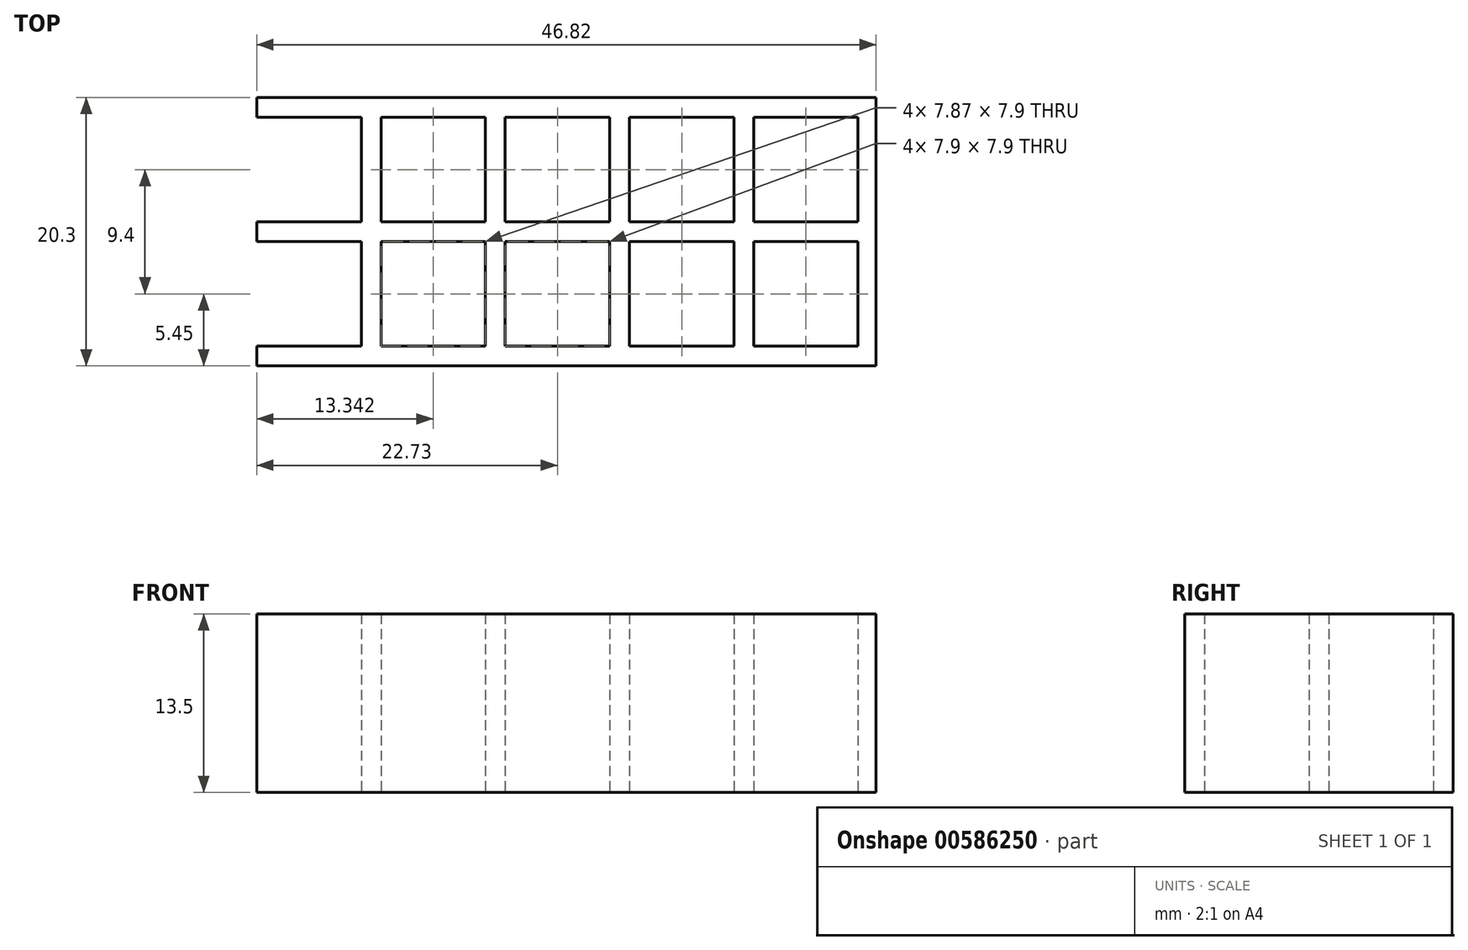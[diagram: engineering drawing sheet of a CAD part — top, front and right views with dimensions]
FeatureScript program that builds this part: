
annotation { "Feature Type Name" : "Feature", "Feature Type Description" : "" }
export const myFeature = defineFeature(function(context is Context, id is Id, definition is map)
    precondition{}
    {
        {
            var Q0;
            Q0=qCreatedBy(makeId("Top.planeOp"),FACE);
            var sketch = newSketch(context, id + "F0", { "sketchPlane" : qUnion([Q0])});
            skLineSegment(sketch, "E0.bottom", {"start": v(-26.67, 20.52) * mm, "end": v(26.68, 20.52) * mm});
            skLineSegment(sketch, "E0.top", {"start": v(-26.68, -20.52) * mm, "end": v(26.67, -20.52) * mm});
            skLineSegment(sketch, "E0.left", {"start": v(-26.67, 20.52) * mm, "end": v(-26.68, -20.53) * mm});
            skLineSegment(sketch, "E0.right", {"start": v(26.68, 20.52) * mm, "end": v(26.67, -20.52) * mm});
            skPoint(sketch, "E0.middle", {"position": v(0, 0) * mm});
            skLineSegment(sketch, "E1.bottom", {"start": v(-26.68, 0.75) * mm, "end": v(26.68, 0.75) * mm});
            skLineSegment(sketch, "E1.top", {"start": v(-26.68, -0.75) * mm, "end": v(26.68, -0.75) * mm});
            skLineSegment(sketch, "E1.left", {"start": v(-26.67, 0.75) * mm, "end": v(-26.67, -0.75) * mm});
            skLineSegment(sketch, "E1.right", {"start": v(26.67, 0.75) * mm, "end": v(26.67, -0.75) * mm});
            skLineSegment(sketch, "E2.bottom", {"start": v(-26.67, -0.75) * mm, "end": v(26.67, -0.75) * mm});
            skLineSegment(sketch, "E2.top", {"start": v(-26.67, -8.65) * mm, "end": v(26.68, -8.65) * mm});
            skLineSegment(sketch, "E2.left", {"start": v(-26.68, -0.75) * mm, "end": v(-26.68, -8.65) * mm});
            skLineSegment(sketch, "E2.right", {"start": v(26.67, -0.75) * mm, "end": v(26.67, -8.65) * mm});
            skLineSegment(sketch, "E3.bottom", {"start": v(-26.67, -8.65) * mm, "end": v(26.67, -8.65) * mm});
            skLineSegment(sketch, "E3.top", {"start": v(-26.68, -10.15) * mm, "end": v(26.68, -10.15) * mm});
            skLineSegment(sketch, "E3.left", {"start": v(-26.67, -8.65) * mm, "end": v(-26.67, -10.15) * mm});
            skLineSegment(sketch, "E3.right", {"start": v(26.67, -8.65) * mm, "end": v(26.67, -10.15) * mm});
            skLineSegment(sketch, "E4", {"start": v(-26.67, -10.15) * mm, "end": v(-26.67, -8.65) * mm});
            skLineSegment(sketch, "E5.top", {"start": v(-26.68, 8.65) * mm, "end": v(26.68, 8.65) * mm});
            skLineSegment(sketch, "E5.left", {"start": v(-26.68, 0.75) * mm, "end": v(-26.68, 8.65) * mm});
            skLineSegment(sketch, "E5.right", {"start": v(26.68, 0.75) * mm, "end": v(26.68, 8.65) * mm});
            skLineSegment(sketch, "E6", {"start": v(-26.68, 8.65) * mm, "end": v(-26.68, 0.75) * mm});
            skLineSegment(sketch, "E7.top", {"start": v(-26.68, 10.15) * mm, "end": v(26.68, 10.15) * mm});
            skLineSegment(sketch, "E7.left", {"start": v(-26.68, 8.65) * mm, "end": v(-26.68, 10.15) * mm});
            skLineSegment(sketch, "E7.right", {"start": v(26.68, 8.65) * mm, "end": v(26.68, 10.15) * mm});
            skLineSegment(sketch, "E8.bottom", {"start": v(-26.67, 20.52) * mm, "end": v(-18.78, 20.52) * mm});
            skLineSegment(sketch, "E8.top", {"start": v(-26.67, -20.52) * mm, "end": v(-18.78, -20.52) * mm});
            skLineSegment(sketch, "E8.left", {"start": v(-26.67, 20.52) * mm, "end": v(-26.67, -20.52) * mm});
            skLineSegment(sketch, "E8.right", {"start": v(-18.78, 20.52) * mm, "end": v(-18.78, -20.53) * mm});
            skLineSegment(sketch, "E9.bottom", {"start": v(-18.78, 20.52) * mm, "end": v(-17.27, 20.52) * mm});
            skLineSegment(sketch, "E9.top", {"start": v(-18.78, -20.52) * mm, "end": v(-17.27, -20.52) * mm});
            skLineSegment(sketch, "E9.left", {"start": v(-18.78, 20.52) * mm, "end": v(-18.78, -20.52) * mm});
            skLineSegment(sketch, "E9.right", {"start": v(-17.27, 20.52) * mm, "end": v(-17.27, -20.53) * mm});
            skLineSegment(sketch, "E10.bottom", {"start": v(-17.27, 20.52) * mm, "end": v(-9.4, 20.52) * mm});
            skLineSegment(sketch, "E10.top", {"start": v(-17.27, -20.52) * mm, "end": v(-9.4, -20.52) * mm});
            skLineSegment(sketch, "E10.left", {"start": v(-17.27, 20.52) * mm, "end": v(-17.27, -20.52) * mm});
            skLineSegment(sketch, "E10.right", {"start": v(-9.4, 20.52) * mm, "end": v(-9.4, -20.53) * mm});
            skLineSegment(sketch, "E11.bottom", {"start": v(-9.4, 20.52) * mm, "end": v(-7.9, 20.52) * mm});
            skLineSegment(sketch, "E11.top", {"start": v(-9.4, -20.52) * mm, "end": v(-7.9, -20.52) * mm});
            skLineSegment(sketch, "E11.right", {"start": v(-7.9, 20.52) * mm, "end": v(-7.9, -20.53) * mm});
            skLineSegment(sketch, "E12.bottom", {"start": v(-7.9, 20.52) * mm, "end": v(0, 20.52) * mm});
            skLineSegment(sketch, "E12.top", {"start": v(-7.9, -20.52) * mm, "end": v(0, -20.52) * mm});
            skLineSegment(sketch, "E12.right", {"start": v(0, 20.52) * mm, "end": v(0, -20.52) * mm});
            skLineSegment(sketch, "E13.bottom", {"start": v(0, 20.52) * mm, "end": v(1.5, 20.52) * mm});
            skLineSegment(sketch, "E13.top", {"start": v(0, -20.52) * mm, "end": v(1.5, -20.52) * mm});
            skLineSegment(sketch, "E13.right", {"start": v(1.5, 20.52) * mm, "end": v(1.5, -20.53) * mm});
            skLineSegment(sketch, "E14.bottom", {"start": v(1.5, 20.52) * mm, "end": v(9.4, 20.52) * mm});
            skLineSegment(sketch, "E14.top", {"start": v(1.5, -20.52) * mm, "end": v(9.4, -20.52) * mm});
            skLineSegment(sketch, "E14.left", {"start": v(1.5, 20.52) * mm, "end": v(1.5, -20.52) * mm});
            skLineSegment(sketch, "E14.right", {"start": v(9.4, 20.52) * mm, "end": v(9.4, -20.53) * mm});
            skLineSegment(sketch, "E15.bottom", {"start": v(9.4, 20.52) * mm, "end": v(10.9, 20.52) * mm});
            skLineSegment(sketch, "E15.top", {"start": v(9.4, -20.52) * mm, "end": v(10.9, -20.52) * mm});
            skLineSegment(sketch, "E15.left", {"start": v(9.4, 20.52) * mm, "end": v(9.4, -20.52) * mm});
            skLineSegment(sketch, "E15.right", {"start": v(10.9, 20.52) * mm, "end": v(10.9, -20.53) * mm});
            skLineSegment(sketch, "E16", {"start": v(10.9, 20.52) * mm, "end": v(9.4, 20.52) * mm, "construction": true});
            skLineSegment(sketch, "E17.bottom", {"start": v(10.9, 20.52) * mm, "end": v(18.78, 20.52) * mm});
            skLineSegment(sketch, "E17.top", {"start": v(10.9, -20.52) * mm, "end": v(18.78, -20.52) * mm});
            skLineSegment(sketch, "E17.left", {"start": v(10.9, 20.52) * mm, "end": v(10.9, -20.52) * mm});
            skLineSegment(sketch, "E17.right", {"start": v(18.78, 20.52) * mm, "end": v(18.78, -20.53) * mm});
            skLineSegment(sketch, "E18.bottom", {"start": v(18.78, 20.52) * mm, "end": v(20.14, 20.52) * mm});
            skLineSegment(sketch, "E18.top", {"start": v(18.78, -20.52) * mm, "end": v(20.14, -20.52) * mm});
            skLineSegment(sketch, "E18.left", {"start": v(18.78, 20.52) * mm, "end": v(18.78, -20.52) * mm});
            skLineSegment(sketch, "E18.right", {"start": v(20.14, 20.52) * mm, "end": v(20.14, -20.52) * mm});
            skSolve(sketch);
        }
        {
            var Q0;
            {var subQ5=sQuery(id+"F0.wireOp",EDGE,"E9.bottom");Q0=makeQuery(id+"F0.imprint","IMPRINT",FACE,{"disambiguationData":[TD([[makeQuery(id+"F0.imprint","IMPRINT",EDGE,{"derivedFrom":subQ5}),-1.0]])]});}
            var Q1;
            {var subQ0=sQuery(id+"F0.wireOp",EDGE,"E9.left");var subQ1=sQuery(id+"F0.wireOp",EDGE,"E5.top");var subQ2=makeQuery(id+"F0.imprint","INTERSECT",VERTEX,{"derivedFrom":[subQ1,subQ0]});Q1=makeQuery(id+"F0.imprint","IMPRINT",FACE,{"disambiguationData":[TD([[makeQuery(id+"F0.imprint","IMPRINT",EDGE,{"disambiguationData":[TD([[subQ2,-1.0]])],"derivedFrom":subQ1}),1.0]])]});}
            var Q2;
            {var subQ0=sQuery(id+"F0.wireOp",EDGE,"E8.left");var subQ1=sQuery(id+"F0.wireOp",EDGE,"E5.top");var subQ2=makeQuery(id+"F0.imprint","INTERSECT",VERTEX,{"derivedFrom":[subQ1,subQ0]});Q2=makeQuery(id+"F0.imprint","IMPRINT",FACE,{"disambiguationData":[TD([[makeQuery(id+"F0.imprint","IMPRINT",EDGE,{"disambiguationData":[TD([[subQ2,-1.0]])],"derivedFrom":subQ1}),1.0]])]});}
            var Q3;
            {var subQ0=sQuery(id+"F0.wireOp",EDGE,"E9.left");var subQ1=sQuery(id+"F0.wireOp",EDGE,"E1.bottom");var subQ2=makeQuery(id+"F0.imprint","INTERSECT",VERTEX,{"derivedFrom":[subQ1,subQ0]});Q3=makeQuery(id+"F0.imprint","IMPRINT",FACE,{"disambiguationData":[TD([[makeQuery(id+"F0.imprint","IMPRINT",EDGE,{"disambiguationData":[TD([[subQ2,-1.0]])],"derivedFrom":subQ1}),1.0]])]});}
            var Q4;
            {var subQ0=sQuery(id+"F0.wireOp",EDGE,"E9.left");var subQ1=sQuery(id+"F0.wireOp",EDGE,"E2.bottom");var subQ2=makeQuery(id+"F0.imprint","INTERSECT",VERTEX,{"derivedFrom":[subQ1,subQ0]});Q4=makeQuery(id+"F0.imprint","IMPRINT",FACE,{"disambiguationData":[TD([[makeQuery(id+"F0.imprint","IMPRINT",EDGE,{"disambiguationData":[TD([[subQ2,-1.0]])],"derivedFrom":subQ1}),1.0]])]});}
            var Q5;
            {var subQ0=sQuery(id+"F0.wireOp",EDGE,"E8.left");var subQ1=sQuery(id+"F0.wireOp",EDGE,"E2.bottom");var subQ2=makeQuery(id+"F0.imprint","INTERSECT",VERTEX,{"derivedFrom":[subQ1,subQ0]});Q5=makeQuery(id+"F0.imprint","IMPRINT",FACE,{"disambiguationData":[TD([[makeQuery(id+"F0.imprint","IMPRINT",EDGE,{"disambiguationData":[TD([[subQ2,-1.0]])],"derivedFrom":subQ1}),1.0]])]});}
            var Q6;
            {var subQ0=sQuery(id+"F0.wireOp",EDGE,"E9.left");var subQ1=sQuery(id+"F0.wireOp",EDGE,"E2.bottom");var subQ2=makeQuery(id+"F0.imprint","INTERSECT",VERTEX,{"derivedFrom":[subQ1,subQ0]});Q6=makeQuery(id+"F0.imprint","IMPRINT",FACE,{"disambiguationData":[TD([[makeQuery(id+"F0.imprint","IMPRINT",EDGE,{"disambiguationData":[TD([[subQ2,-1.0]])],"derivedFrom":subQ1}),-1.0]])]});}
            var Q7;
            {var subQ0=sQuery(id+"F0.wireOp",EDGE,"E9.left");var subQ1=sQuery(id+"F0.wireOp",EDGE,"E3.bottom");var subQ2=makeQuery(id+"F0.imprint","INTERSECT",VERTEX,{"derivedFrom":[subQ1,subQ0]});Q7=makeQuery(id+"F0.imprint","IMPRINT",FACE,{"disambiguationData":[TD([[makeQuery(id+"F0.imprint","IMPRINT",EDGE,{"disambiguationData":[TD([[subQ2,-1.0]])],"derivedFrom":subQ1}),-1.0]])]});}
            var Q8;
            {var subQ0=sQuery(id+"F0.wireOp",EDGE,"E8.left");var subQ1=sQuery(id+"F0.wireOp",EDGE,"E3.bottom");var subQ2=makeQuery(id+"F0.imprint","INTERSECT",VERTEX,{"derivedFrom":[subQ1,subQ0]});Q8=makeQuery(id+"F0.imprint","IMPRINT",FACE,{"disambiguationData":[TD([[makeQuery(id+"F0.imprint","IMPRINT",EDGE,{"disambiguationData":[TD([[subQ2,-1.0]])],"derivedFrom":subQ1}),-1.0]])]});}
            var Q9;
            {var subQ5=sQuery(id+"F0.wireOp",EDGE,"E9.top");Q9=makeQuery(id+"F0.imprint","IMPRINT",FACE,{"disambiguationData":[TD([[makeQuery(id+"F0.imprint","IMPRINT",EDGE,{"derivedFrom":subQ5}),1.0]])]});}
            var Q10;
            {var subQ0=sQuery(id+"F0.wireOp",EDGE,"E10.left");var subQ1=sQuery(id+"F0.wireOp",EDGE,"E3.bottom");var subQ2=makeQuery(id+"F0.imprint","INTERSECT",VERTEX,{"derivedFrom":[subQ1,subQ0]});Q10=makeQuery(id+"F0.imprint","IMPRINT",FACE,{"disambiguationData":[TD([[makeQuery(id+"F0.imprint","IMPRINT",EDGE,{"disambiguationData":[TD([[subQ2,-1.0]])],"derivedFrom":subQ1}),-1.0]])]});}
            var Q11;
            {var subQ0=sQuery(id+"F0.wireOp",EDGE,"E10.right");var subQ1=sQuery(id+"F0.wireOp",EDGE,"E3.bottom");var subQ2=makeQuery(id+"F0.imprint","INTERSECT",VERTEX,{"derivedFrom":[subQ1,subQ0]});Q11=makeQuery(id+"F0.imprint","IMPRINT",FACE,{"disambiguationData":[TD([[makeQuery(id+"F0.imprint","IMPRINT",EDGE,{"disambiguationData":[TD([[subQ2,-1.0]])],"derivedFrom":subQ1}),-1.0]])]});}
            var Q12;
            {var subQ0=sQuery(id+"F0.wireOp",EDGE,"E10.right");var subQ1=sQuery(id+"F0.wireOp",EDGE,"E2.bottom");var subQ2=makeQuery(id+"F0.imprint","INTERSECT",VERTEX,{"derivedFrom":[subQ1,subQ0]});Q12=makeQuery(id+"F0.imprint","IMPRINT",FACE,{"disambiguationData":[TD([[makeQuery(id+"F0.imprint","IMPRINT",EDGE,{"disambiguationData":[TD([[subQ2,-1.0]])],"derivedFrom":subQ1}),-1.0]])]});}
            var Q13;
            {var subQ0=sQuery(id+"F0.wireOp",EDGE,"E10.right");var subQ1=sQuery(id+"F0.wireOp",EDGE,"E2.bottom");var subQ2=makeQuery(id+"F0.imprint","INTERSECT",VERTEX,{"derivedFrom":[subQ1,subQ0]});Q13=makeQuery(id+"F0.imprint","IMPRINT",FACE,{"disambiguationData":[TD([[makeQuery(id+"F0.imprint","IMPRINT",EDGE,{"disambiguationData":[TD([[subQ2,-1.0]])],"derivedFrom":subQ1}),1.0]])]});}
            var Q14;
            {var subQ0=sQuery(id+"F0.wireOp",EDGE,"E10.left");var subQ1=sQuery(id+"F0.wireOp",EDGE,"E2.bottom");var subQ2=makeQuery(id+"F0.imprint","INTERSECT",VERTEX,{"derivedFrom":[subQ1,subQ0]});Q14=makeQuery(id+"F0.imprint","IMPRINT",FACE,{"disambiguationData":[TD([[makeQuery(id+"F0.imprint","IMPRINT",EDGE,{"disambiguationData":[TD([[subQ2,-1.0]])],"derivedFrom":subQ1}),1.0]])]});}
            var Q15;
            {var subQ5=sQuery(id+"F0.wireOp",EDGE,"E11.top");Q15=makeQuery(id+"F0.imprint","IMPRINT",FACE,{"disambiguationData":[TD([[makeQuery(id+"F0.imprint","IMPRINT",EDGE,{"derivedFrom":subQ5}),1.0]])]});}
            var Q16;
            {var subQ5=sQuery(id+"F0.wireOp",EDGE,"E11.bottom");Q16=makeQuery(id+"F0.imprint","IMPRINT",FACE,{"disambiguationData":[TD([[makeQuery(id+"F0.imprint","IMPRINT",EDGE,{"derivedFrom":subQ5}),-1.0]])]});}
            var Q17;
            {var subQ0=sQuery(id+"F0.wireOp",EDGE,"E10.right");var subQ1=sQuery(id+"F0.wireOp",EDGE,"E5.top");var subQ2=makeQuery(id+"F0.imprint","INTERSECT",VERTEX,{"derivedFrom":[subQ1,subQ0]});Q17=makeQuery(id+"F0.imprint","IMPRINT",FACE,{"disambiguationData":[TD([[makeQuery(id+"F0.imprint","IMPRINT",EDGE,{"disambiguationData":[TD([[subQ2,-1.0]])],"derivedFrom":subQ1}),1.0]])]});}
            var Q18;
            {var subQ0=sQuery(id+"F0.wireOp",EDGE,"E10.right");var subQ1=sQuery(id+"F0.wireOp",EDGE,"E1.bottom");var subQ2=makeQuery(id+"F0.imprint","INTERSECT",VERTEX,{"derivedFrom":[subQ1,subQ0]});Q18=makeQuery(id+"F0.imprint","IMPRINT",FACE,{"disambiguationData":[TD([[makeQuery(id+"F0.imprint","IMPRINT",EDGE,{"disambiguationData":[TD([[subQ2,-1.0]])],"derivedFrom":subQ1}),1.0]])]});}
            var Q19;
            {var subQ0=sQuery(id+"F0.wireOp",EDGE,"E10.left");var subQ1=sQuery(id+"F0.wireOp",EDGE,"E5.top");var subQ2=makeQuery(id+"F0.imprint","INTERSECT",VERTEX,{"derivedFrom":[subQ1,subQ0]});Q19=makeQuery(id+"F0.imprint","IMPRINT",FACE,{"disambiguationData":[TD([[makeQuery(id+"F0.imprint","IMPRINT",EDGE,{"disambiguationData":[TD([[subQ2,-1.0]])],"derivedFrom":subQ1}),1.0]])]});}
            var Q20;
            {var subQ0=sQuery(id+"F0.wireOp",EDGE,"E11.right");var subQ1=sQuery(id+"F0.wireOp",EDGE,"E5.top");var subQ2=makeQuery(id+"F0.imprint","INTERSECT",VERTEX,{"derivedFrom":[subQ1,subQ0]});Q20=makeQuery(id+"F0.imprint","IMPRINT",FACE,{"disambiguationData":[TD([[makeQuery(id+"F0.imprint","IMPRINT",EDGE,{"disambiguationData":[TD([[subQ2,-1.0]])],"derivedFrom":subQ1}),1.0]])]});}
            var Q21;
            {var subQ0=sQuery(id+"F0.wireOp",EDGE,"E12.right");var subQ1=sQuery(id+"F0.wireOp",EDGE,"E5.top");var subQ2=makeQuery(id+"F0.imprint","INTERSECT",VERTEX,{"derivedFrom":[subQ1,subQ0]});Q21=makeQuery(id+"F0.imprint","IMPRINT",FACE,{"disambiguationData":[TD([[makeQuery(id+"F0.imprint","IMPRINT",EDGE,{"disambiguationData":[TD([[subQ2,-1.0]])],"derivedFrom":subQ1}),1.0]])]});}
            var Q22;
            {var subQ5=sQuery(id+"F0.wireOp",EDGE,"E13.bottom");Q22=makeQuery(id+"F0.imprint","IMPRINT",FACE,{"disambiguationData":[TD([[makeQuery(id+"F0.imprint","IMPRINT",EDGE,{"derivedFrom":subQ5}),-1.0]])]});}
            var Q23;
            {var subQ0=sQuery(id+"F0.wireOp",EDGE,"E12.right");var subQ1=sQuery(id+"F0.wireOp",EDGE,"E1.bottom");var subQ2=makeQuery(id+"F0.imprint","INTERSECT",VERTEX,{"derivedFrom":[subQ1,subQ0]});Q23=makeQuery(id+"F0.imprint","IMPRINT",FACE,{"disambiguationData":[TD([[makeQuery(id+"F0.imprint","IMPRINT",EDGE,{"disambiguationData":[TD([[subQ2,-1.0]])],"derivedFrom":subQ1}),1.0]])]});}
            var Q24;
            {var subQ0=sQuery(id+"F0.wireOp",EDGE,"E11.right");var subQ1=sQuery(id+"F0.wireOp",EDGE,"E2.bottom");var subQ2=makeQuery(id+"F0.imprint","INTERSECT",VERTEX,{"derivedFrom":[subQ1,subQ0]});Q24=makeQuery(id+"F0.imprint","IMPRINT",FACE,{"disambiguationData":[TD([[makeQuery(id+"F0.imprint","IMPRINT",EDGE,{"disambiguationData":[TD([[subQ2,-1.0]])],"derivedFrom":subQ1}),1.0]])]});}
            var Q25;
            {var subQ0=sQuery(id+"F0.wireOp",EDGE,"E12.right");var subQ1=sQuery(id+"F0.wireOp",EDGE,"E2.bottom");var subQ2=makeQuery(id+"F0.imprint","INTERSECT",VERTEX,{"derivedFrom":[subQ1,subQ0]});Q25=makeQuery(id+"F0.imprint","IMPRINT",FACE,{"disambiguationData":[TD([[makeQuery(id+"F0.imprint","IMPRINT",EDGE,{"disambiguationData":[TD([[subQ2,-1.0]])],"derivedFrom":subQ1}),1.0]])]});}
            var Q26;
            {var subQ0=sQuery(id+"F0.wireOp",EDGE,"E12.right");var subQ1=sQuery(id+"F0.wireOp",EDGE,"E2.bottom");var subQ2=makeQuery(id+"F0.imprint","INTERSECT",VERTEX,{"derivedFrom":[subQ1,subQ0]});Q26=makeQuery(id+"F0.imprint","IMPRINT",FACE,{"disambiguationData":[TD([[makeQuery(id+"F0.imprint","IMPRINT",EDGE,{"disambiguationData":[TD([[subQ2,-1.0]])],"derivedFrom":subQ1}),-1.0]])]});}
            var Q27;
            {var subQ0=sQuery(id+"F0.wireOp",EDGE,"E12.right");var subQ1=sQuery(id+"F0.wireOp",EDGE,"E3.bottom");var subQ2=makeQuery(id+"F0.imprint","INTERSECT",VERTEX,{"derivedFrom":[subQ1,subQ0]});Q27=makeQuery(id+"F0.imprint","IMPRINT",FACE,{"disambiguationData":[TD([[makeQuery(id+"F0.imprint","IMPRINT",EDGE,{"disambiguationData":[TD([[subQ2,-1.0]])],"derivedFrom":subQ1}),-1.0]])]});}
            var Q28;
            {var subQ0=sQuery(id+"F0.wireOp",EDGE,"E11.right");var subQ1=sQuery(id+"F0.wireOp",EDGE,"E3.bottom");var subQ2=makeQuery(id+"F0.imprint","INTERSECT",VERTEX,{"derivedFrom":[subQ1,subQ0]});Q28=makeQuery(id+"F0.imprint","IMPRINT",FACE,{"disambiguationData":[TD([[makeQuery(id+"F0.imprint","IMPRINT",EDGE,{"disambiguationData":[TD([[subQ2,-1.0]])],"derivedFrom":subQ1}),-1.0]])]});}
            var Q29;
            {var subQ5=sQuery(id+"F0.wireOp",EDGE,"E13.top");Q29=makeQuery(id+"F0.imprint","IMPRINT",FACE,{"disambiguationData":[TD([[makeQuery(id+"F0.imprint","IMPRINT",EDGE,{"derivedFrom":subQ5}),1.0]])]});}
            var Q30;
            {var subQ0=sQuery(id+"F0.wireOp",EDGE,"E14.left");var subQ1=sQuery(id+"F0.wireOp",EDGE,"E3.bottom");var subQ2=makeQuery(id+"F0.imprint","INTERSECT",VERTEX,{"derivedFrom":[subQ1,subQ0]});Q30=makeQuery(id+"F0.imprint","IMPRINT",FACE,{"disambiguationData":[TD([[makeQuery(id+"F0.imprint","IMPRINT",EDGE,{"disambiguationData":[TD([[subQ2,-1.0]])],"derivedFrom":subQ1}),-1.0]])]});}
            var Q31;
            {var subQ5=sQuery(id+"F0.wireOp",EDGE,"E15.top");Q31=makeQuery(id+"F0.imprint","IMPRINT",FACE,{"disambiguationData":[TD([[makeQuery(id+"F0.imprint","IMPRINT",EDGE,{"derivedFrom":subQ5}),1.0]])]});}
            var Q32;
            {var subQ5=sQuery(id+"F0.wireOp",EDGE,"E18.top");Q32=makeQuery(id+"F0.imprint","IMPRINT",FACE,{"disambiguationData":[TD([[makeQuery(id+"F0.imprint","IMPRINT",EDGE,{"derivedFrom":subQ5}),1.0]])]});}
            var Q33;
            {var subQ0=sQuery(id+"F0.wireOp",EDGE,"E3.right");Q33=makeQuery(id+"F0.imprint","IMPRINT",FACE,{"disambiguationData":[TD([[makeQuery(id+"F0.imprint","IMPRINT",EDGE,{"derivedFrom":subQ0}),-1.0]])]});}
            var Q34;
            {var subQ0=sQuery(id+"F0.wireOp",EDGE,"E17.left");var subQ1=sQuery(id+"F0.wireOp",EDGE,"E3.bottom");var subQ2=makeQuery(id+"F0.imprint","INTERSECT",VERTEX,{"derivedFrom":[subQ1,subQ0]});Q34=makeQuery(id+"F0.imprint","IMPRINT",FACE,{"disambiguationData":[TD([[makeQuery(id+"F0.imprint","IMPRINT",EDGE,{"disambiguationData":[TD([[subQ2,-1.0]])],"derivedFrom":subQ1}),-1.0]])]});}
            var Q35;
            {var subQ0=sQuery(id+"F0.wireOp",EDGE,"E18.left");var subQ1=sQuery(id+"F0.wireOp",EDGE,"E3.bottom");var subQ2=makeQuery(id+"F0.imprint","INTERSECT",VERTEX,{"derivedFrom":[subQ1,subQ0]});Q35=makeQuery(id+"F0.imprint","IMPRINT",FACE,{"disambiguationData":[TD([[makeQuery(id+"F0.imprint","IMPRINT",EDGE,{"disambiguationData":[TD([[subQ2,-1.0]])],"derivedFrom":subQ1}),-1.0]])]});}
            var Q36;
            {var subQ0=sQuery(id+"F0.wireOp",EDGE,"E15.left");var subQ1=sQuery(id+"F0.wireOp",EDGE,"E3.bottom");var subQ2=makeQuery(id+"F0.imprint","INTERSECT",VERTEX,{"derivedFrom":[subQ1,subQ0]});Q36=makeQuery(id+"F0.imprint","IMPRINT",FACE,{"disambiguationData":[TD([[makeQuery(id+"F0.imprint","IMPRINT",EDGE,{"disambiguationData":[TD([[subQ2,-1.0]])],"derivedFrom":subQ1}),-1.0]])]});}
            var Q37;
            {var subQ0=sQuery(id+"F0.wireOp",EDGE,"E15.left");var subQ1=sQuery(id+"F0.wireOp",EDGE,"E2.bottom");var subQ2=makeQuery(id+"F0.imprint","INTERSECT",VERTEX,{"derivedFrom":[subQ1,subQ0]});Q37=makeQuery(id+"F0.imprint","IMPRINT",FACE,{"disambiguationData":[TD([[makeQuery(id+"F0.imprint","IMPRINT",EDGE,{"disambiguationData":[TD([[subQ2,-1.0]])],"derivedFrom":subQ1}),-1.0]])]});}
            var Q38;
            {var subQ0=sQuery(id+"F0.wireOp",EDGE,"E18.left");var subQ1=sQuery(id+"F0.wireOp",EDGE,"E2.bottom");var subQ2=makeQuery(id+"F0.imprint","INTERSECT",VERTEX,{"derivedFrom":[subQ1,subQ0]});Q38=makeQuery(id+"F0.imprint","IMPRINT",FACE,{"disambiguationData":[TD([[makeQuery(id+"F0.imprint","IMPRINT",EDGE,{"disambiguationData":[TD([[subQ2,-1.0]])],"derivedFrom":subQ1}),-1.0]])]});}
            var Q39;
            {var subQ0=sQuery(id+"F0.wireOp",EDGE,"E18.left");var subQ1=sQuery(id+"F0.wireOp",EDGE,"E2.bottom");var subQ2=makeQuery(id+"F0.imprint","INTERSECT",VERTEX,{"derivedFrom":[subQ1,subQ0]});Q39=makeQuery(id+"F0.imprint","IMPRINT",FACE,{"disambiguationData":[TD([[makeQuery(id+"F0.imprint","IMPRINT",EDGE,{"disambiguationData":[TD([[subQ2,-1.0]])],"derivedFrom":subQ1}),1.0]])]});}
            var Q40;
            {var subQ0=sQuery(id+"F0.wireOp",EDGE,"E17.left");var subQ1=sQuery(id+"F0.wireOp",EDGE,"E2.bottom");var subQ2=makeQuery(id+"F0.imprint","INTERSECT",VERTEX,{"derivedFrom":[subQ1,subQ0]});Q40=makeQuery(id+"F0.imprint","IMPRINT",FACE,{"disambiguationData":[TD([[makeQuery(id+"F0.imprint","IMPRINT",EDGE,{"disambiguationData":[TD([[subQ2,-1.0]])],"derivedFrom":subQ1}),1.0]])]});}
            var Q41;
            {var subQ0=sQuery(id+"F0.wireOp",EDGE,"E15.left");var subQ1=sQuery(id+"F0.wireOp",EDGE,"E2.bottom");var subQ2=makeQuery(id+"F0.imprint","INTERSECT",VERTEX,{"derivedFrom":[subQ1,subQ0]});Q41=makeQuery(id+"F0.imprint","IMPRINT",FACE,{"disambiguationData":[TD([[makeQuery(id+"F0.imprint","IMPRINT",EDGE,{"disambiguationData":[TD([[subQ2,-1.0]])],"derivedFrom":subQ1}),1.0]])]});}
            var Q42;
            {var subQ0=sQuery(id+"F0.wireOp",EDGE,"E14.left");var subQ1=sQuery(id+"F0.wireOp",EDGE,"E2.bottom");var subQ2=makeQuery(id+"F0.imprint","INTERSECT",VERTEX,{"derivedFrom":[subQ1,subQ0]});Q42=makeQuery(id+"F0.imprint","IMPRINT",FACE,{"disambiguationData":[TD([[makeQuery(id+"F0.imprint","IMPRINT",EDGE,{"disambiguationData":[TD([[subQ2,-1.0]])],"derivedFrom":subQ1}),1.0]])]});}
            var Q43;
            {var subQ0=sQuery(id+"F0.wireOp",EDGE,"E18.left");var subQ1=sQuery(id+"F0.wireOp",EDGE,"E1.bottom");var subQ2=makeQuery(id+"F0.imprint","INTERSECT",VERTEX,{"derivedFrom":[subQ1,subQ0]});Q43=makeQuery(id+"F0.imprint","IMPRINT",FACE,{"disambiguationData":[TD([[makeQuery(id+"F0.imprint","IMPRINT",EDGE,{"disambiguationData":[TD([[subQ2,-1.0]])],"derivedFrom":subQ1}),1.0]])]});}
            var Q44;
            {var subQ0=sQuery(id+"F0.wireOp",EDGE,"E15.left");var subQ1=sQuery(id+"F0.wireOp",EDGE,"E1.bottom");var subQ2=makeQuery(id+"F0.imprint","INTERSECT",VERTEX,{"derivedFrom":[subQ1,subQ0]});Q44=makeQuery(id+"F0.imprint","IMPRINT",FACE,{"disambiguationData":[TD([[makeQuery(id+"F0.imprint","IMPRINT",EDGE,{"disambiguationData":[TD([[subQ2,-1.0]])],"derivedFrom":subQ1}),1.0]])]});}
            var Q45;
            {var subQ0=sQuery(id+"F0.wireOp",EDGE,"E1.right");Q45=makeQuery(id+"F0.imprint","IMPRINT",FACE,{"disambiguationData":[TD([[makeQuery(id+"F0.imprint","IMPRINT",EDGE,{"derivedFrom":subQ0}),-1.0]])]});}
            var Q46;
            {var subQ0=sQuery(id+"F0.wireOp",EDGE,"E7.right");Q46=makeQuery(id+"F0.imprint","IMPRINT",FACE,{"disambiguationData":[TD([[makeQuery(id+"F0.imprint","IMPRINT",EDGE,{"derivedFrom":subQ0}),1.0]])]});}
            var Q47;
            {var subQ0=sQuery(id+"F0.wireOp",EDGE,"E17.left");var subQ1=sQuery(id+"F0.wireOp",EDGE,"E5.top");var subQ2=makeQuery(id+"F0.imprint","INTERSECT",VERTEX,{"derivedFrom":[subQ1,subQ0]});Q47=makeQuery(id+"F0.imprint","IMPRINT",FACE,{"disambiguationData":[TD([[makeQuery(id+"F0.imprint","IMPRINT",EDGE,{"disambiguationData":[TD([[subQ2,-1.0]])],"derivedFrom":subQ1}),1.0]])]});}
            var Q48;
            {var subQ0=sQuery(id+"F0.wireOp",EDGE,"E18.left");var subQ1=sQuery(id+"F0.wireOp",EDGE,"E5.top");var subQ2=makeQuery(id+"F0.imprint","INTERSECT",VERTEX,{"derivedFrom":[subQ1,subQ0]});Q48=makeQuery(id+"F0.imprint","IMPRINT",FACE,{"disambiguationData":[TD([[makeQuery(id+"F0.imprint","IMPRINT",EDGE,{"disambiguationData":[TD([[subQ2,-1.0]])],"derivedFrom":subQ1}),1.0]])]});}
            var Q49;
            {var subQ5=sQuery(id+"F0.wireOp",EDGE,"E18.bottom");Q49=makeQuery(id+"F0.imprint","IMPRINT",FACE,{"disambiguationData":[TD([[makeQuery(id+"F0.imprint","IMPRINT",EDGE,{"derivedFrom":subQ5}),-1.0]])]});}
            var Q50;
            {var subQ5=sQuery(id+"F0.wireOp",EDGE,"E15.bottom");Q50=makeQuery(id+"F0.imprint","IMPRINT",FACE,{"disambiguationData":[TD([[makeQuery(id+"F0.imprint","IMPRINT",EDGE,{"derivedFrom":subQ5}),-1.0]])]});}
            var Q51;
            {var subQ0=sQuery(id+"F0.wireOp",EDGE,"E15.left");var subQ1=sQuery(id+"F0.wireOp",EDGE,"E5.top");var subQ2=makeQuery(id+"F0.imprint","INTERSECT",VERTEX,{"derivedFrom":[subQ1,subQ0]});Q51=makeQuery(id+"F0.imprint","IMPRINT",FACE,{"disambiguationData":[TD([[makeQuery(id+"F0.imprint","IMPRINT",EDGE,{"disambiguationData":[TD([[subQ2,-1.0]])],"derivedFrom":subQ1}),1.0]])]});}
            var Q52;
            {var subQ0=sQuery(id+"F0.wireOp",EDGE,"E14.left");var subQ1=sQuery(id+"F0.wireOp",EDGE,"E5.top");var subQ2=makeQuery(id+"F0.imprint","INTERSECT",VERTEX,{"derivedFrom":[subQ1,subQ0]});Q52=makeQuery(id+"F0.imprint","IMPRINT",FACE,{"disambiguationData":[TD([[makeQuery(id+"F0.imprint","IMPRINT",EDGE,{"disambiguationData":[TD([[subQ2,-1.0]])],"derivedFrom":subQ1}),1.0]])]});}
            extrude(context, id + "F1", {"entities" : qUnion([Q0, Q1, Q2, Q3, Q4, Q5, Q6, Q7, Q8, Q9, Q10, Q11, Q12, Q13, Q14, Q15, Q16, Q17, Q18, Q19, Q20, Q21, Q22, Q23, Q24, Q25, Q26, Q27, Q28, Q29, Q30, Q31, Q32, Q33, Q34, Q35, Q36, Q37, Q38, Q39, Q40, Q41, Q42, Q43, Q44, Q45, Q46, Q47, Q48, Q49, Q50, Q51, Q52]), "depth" : 13.5 * mm, "offsetDistance" : 25 * mm});
        }
    });
